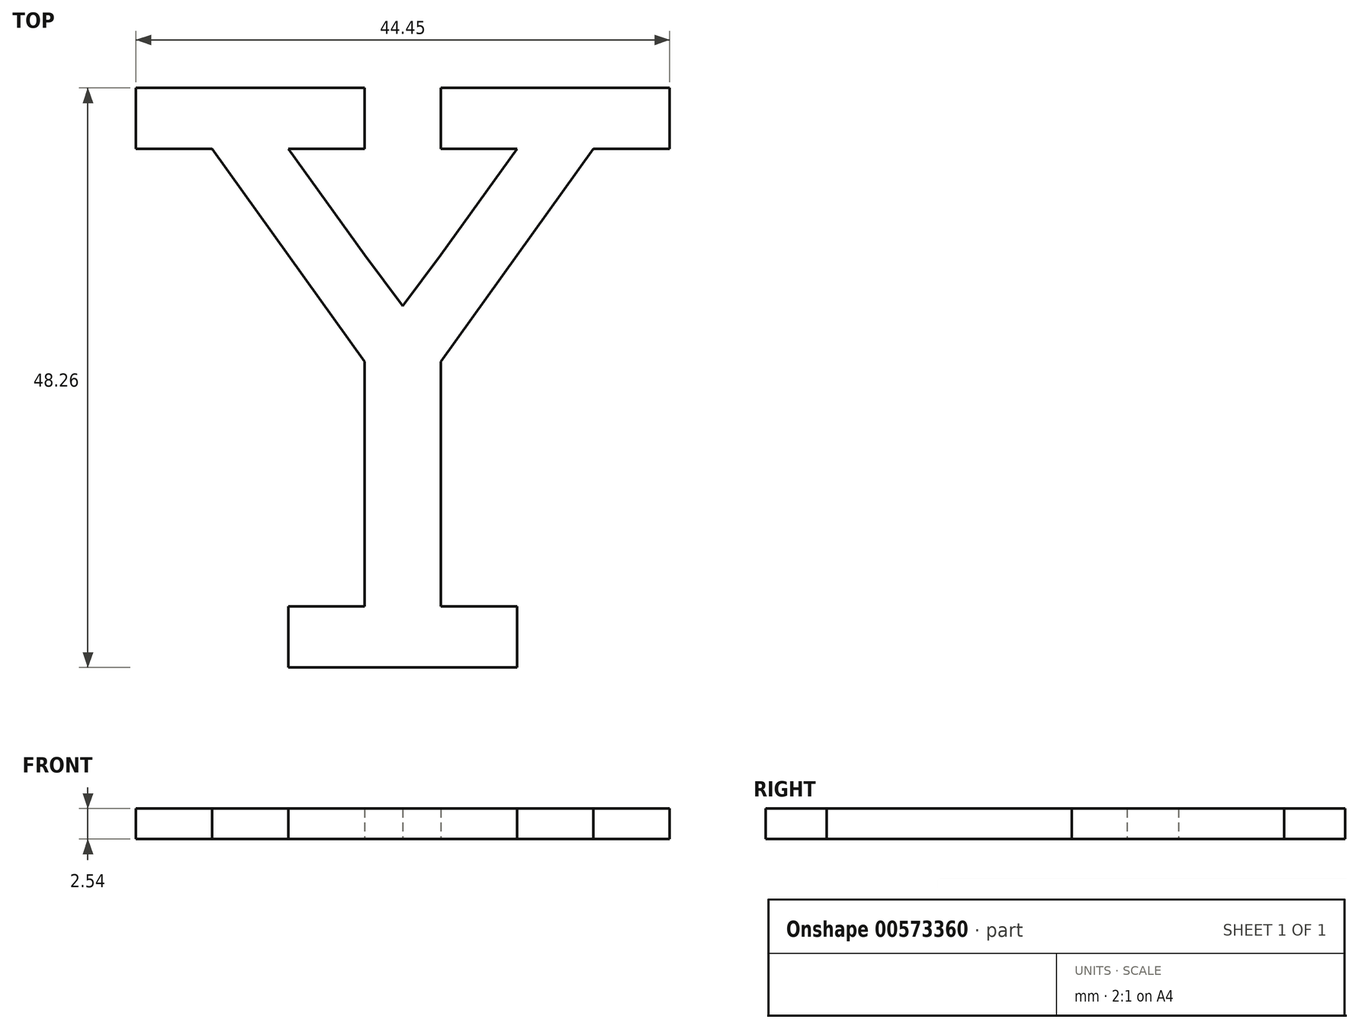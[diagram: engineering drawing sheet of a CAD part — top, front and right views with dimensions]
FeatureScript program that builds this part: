
annotation { "Feature Type Name" : "Feature", "Feature Type Description" : "" }
export const myFeature = defineFeature(function(context is Context, id is Id, definition is map)
    precondition{}
    {
        {
            var Q0;
            Q0=qCreatedBy(makeId("Top.planeOp"),FACE);
            var sketch = newSketch(context, id + "F0", { "sketchPlane" : qUnion([Q0])});
            skLineSegment(sketch, "E0", {"start": v(-57.14, 37.34) * mm, "end": v(-38.1, 37.34) * mm});
            skLineSegment(sketch, "E1", {"start": v(-38.1, 37.34) * mm, "end": v(-38.1, 32.26) * mm});
            skLineSegment(sketch, "E2", {"start": v(-38.1, 32.26) * mm, "end": v(-44.44, 32.26) * mm});
            skLineSegment(sketch, "E3", {"start": v(-12.7, 37.34) * mm, "end": v(-12.7, 32.26) * mm});
            skLineSegment(sketch, "E4", {"start": v(-12.7, 32.26) * mm, "end": v(-19.04, 32.26) * mm});
            skLineSegment(sketch, "E5", {"start": v(-31.74, -5.84) * mm, "end": v(-25.4, -5.84) * mm});
            skLineSegment(sketch, "E6", {"start": v(-25.4, -5.84) * mm, "end": v(-25.4, -10.92) * mm});
            skLineSegment(sketch, "E7", {"start": v(-25.4, -10.92) * mm, "end": v(-44.44, -10.92) * mm});
            skLineSegment(sketch, "E8", {"start": v(-44.44, -10.92) * mm, "end": v(-44.44, -5.84) * mm});
            skLineSegment(sketch, "E9", {"start": v(-44.44, -5.84) * mm, "end": v(-38.1, -5.84) * mm});
            skLineSegment(sketch, "E10", {"start": v(-50.8, 32.26) * mm, "end": v(-57.14, 32.26) * mm});
            skLineSegment(sketch, "E11", {"start": v(-57.14, 32.26) * mm, "end": v(-57.14, 37.34) * mm});
            skLineSegment(sketch, "E12", {"start": v(-25.4, 32.26) * mm, "end": v(-31.74, 32.26) * mm});
            skLineSegment(sketch, "E13", {"start": v(-31.74, 32.26) * mm, "end": v(-31.74, 37.34) * mm});
            skLineSegment(sketch, "E14", {"start": v(-31.74, 37.34) * mm, "end": v(-12.7, 37.34) * mm});
            skLineSegment(sketch, "E15", {"start": v(-38.1, -5.84) * mm, "end": v(-38.1, 14.56) * mm});
            skLineSegment(sketch, "E16", {"start": v(-31.74, -5.84) * mm, "end": v(-31.74, 14.56) * mm});
            skLineSegment(sketch, "E17", {"start": v(-50.8, 32.26) * mm, "end": v(-38.1, 14.56) * mm});
            skLineSegment(sketch, "E18", {"start": v(-19.04, 32.26) * mm, "end": v(-31.74, 14.56) * mm});
            skLineSegment(sketch, "E19", {"start": v(-44.44, 32.26) * mm, "end": v(-38.1, 23.45) * mm});
            skLineSegment(sketch, "E20", {"start": v(-25.4, 32.26) * mm, "end": v(-31.74, 23.45) * mm});
            skLineSegment(sketch, "E21", {"start": v(-38.1, 23.45) * mm, "end": v(-34.92, 19.17) * mm});
            skLineSegment(sketch, "E22", {"start": v(-34.92, 19.17) * mm, "end": v(-31.74, 23.45) * mm});
            skSolve(sketch);
        }
        {
            var Q0;
            Q0 = qSketchRegion(id + "F0", true);
            extrude(context, id + "F1", {"entities" : qUnion([Q0]), "depth" : 2.54 * mm, "offsetDistance" : 25.4 * mm});
        }
    });
